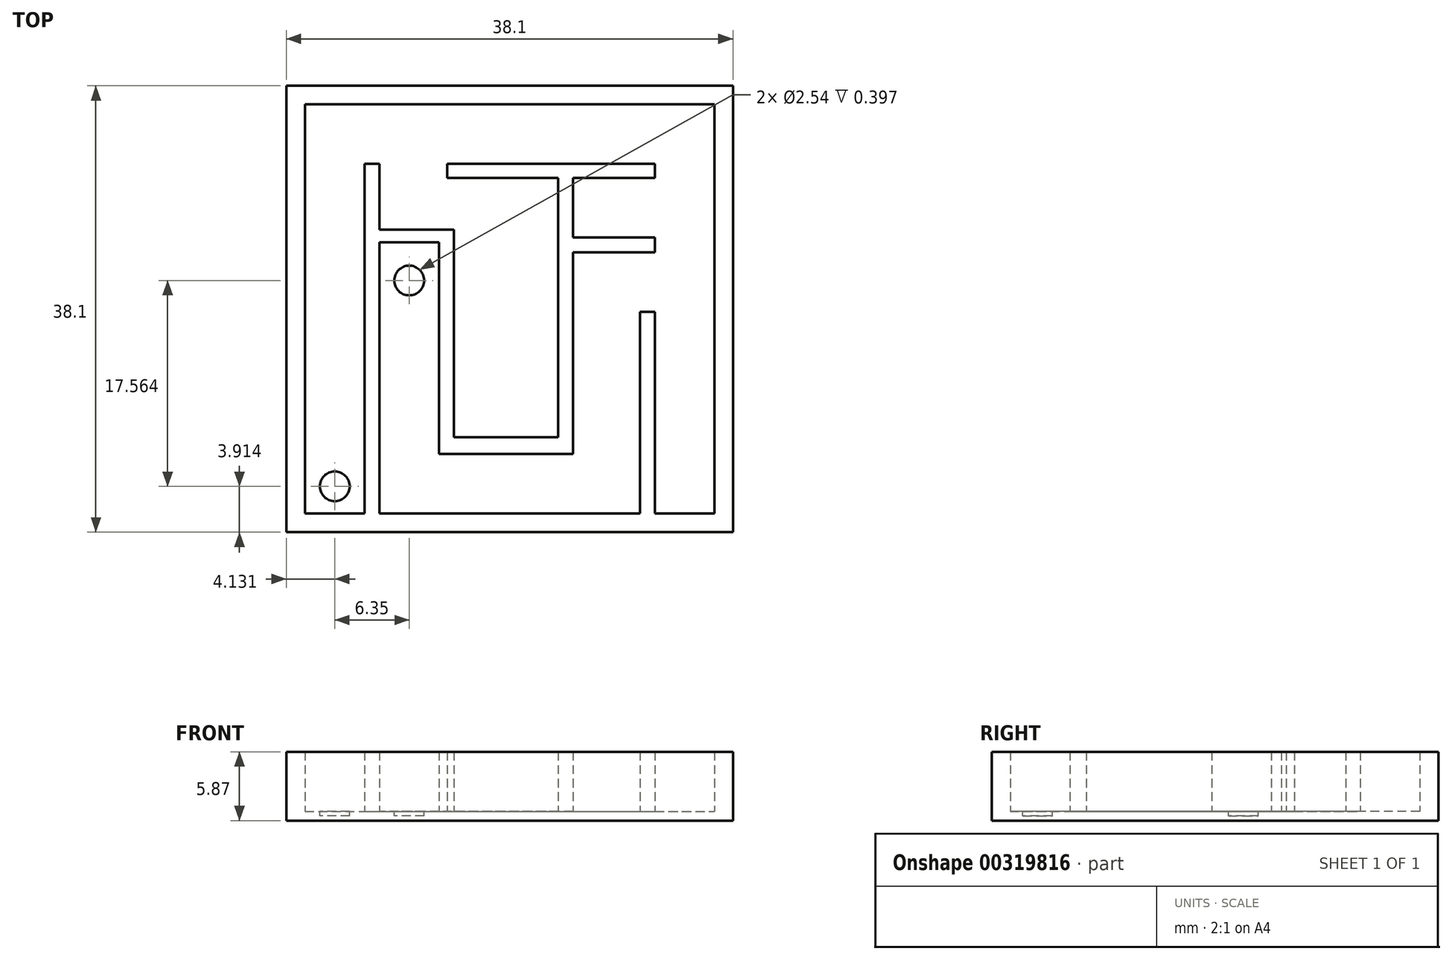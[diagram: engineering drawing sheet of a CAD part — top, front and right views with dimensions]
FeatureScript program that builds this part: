
annotation { "Feature Type Name" : "Feature", "Feature Type Description" : "" }
export const myFeature = defineFeature(function(context is Context, id is Id, definition is map)
    precondition{}
    {
        {
            var Q0;
            Q0=qCreatedBy(makeId("Top.planeOp"),FACE);
            var sketch = newSketch(context, id + "F0", { "sketchPlane" : qUnion([Q0])});
            skLineSegment(sketch, "E0.bottom", {"start": v(-35.55, 3.52) * mm, "end": v(2.55, 3.52) * mm});
            skLineSegment(sketch, "E0.top", {"start": v(-35.55, -34.58) * mm, "end": v(2.55, -34.58) * mm});
            skLineSegment(sketch, "E0.left", {"start": v(-35.55, 3.52) * mm, "end": v(-35.55, -34.58) * mm});
            skLineSegment(sketch, "E0.right", {"start": v(2.55, 3.52) * mm, "end": v(2.55, -34.58) * mm});
            skSolve(sketch);
        }
        {
            var Q0;
            Q0=makeQuery(id+"F0.imprint","IMPRINT",FACE,{"disambiguationData":[TD([[makeQuery(id+"F0.imprint","IMPRINT",EDGE,{"derivedFrom":sQuery(id+"F0.wireOp",EDGE,"E0.bottom")}),-1.0]])]});
            extrude(context, id + "F1", {"entities" : qUnion([Q0]), "depth" : 0.8 * mm});
        }
        {
            var Q0;
            Q0=makeQuery(id+"F1.opExtrude","CAP_FACE",FACE,{"disambiguationData":[OSD([sQuery(id+"F0.wireOp",EDGE,"E0.bottom"),sQuery(id+"F0.wireOp",EDGE,"E0.top"),sQuery(id+"F0.wireOp",EDGE,"E0.left"),sQuery(id+"F0.wireOp",EDGE,"E0.right")])],"isStart":false});
            var sketch = newSketch(context, id + "F2", { "sketchPlane" : qUnion([Q0])});
            skLineSegment(sketch, "E1.0", {"start": v(-33.96, 1.94) * mm, "end": v(0.97, 1.94) * mm});
            skLineSegment(sketch, "E1.1", {"start": v(-33.96, 1.94) * mm, "end": v(-33.96, -32.99) * mm});
            skLineSegment(sketch, "E1.2", {"start": v(-33.96, -32.99) * mm, "end": v(0.97, -32.99) * mm});
            skLineSegment(sketch, "E1.3", {"start": v(0.97, 1.94) * mm, "end": v(0.97, -32.99) * mm});
            skSolve(sketch);
        }
        {
            var Q0;
            Q0=makeQuery(id+"F2.imprint","IMPRINT",FACE,{"disambiguationData":[TD([[makeQuery(id+"F2.imprint","IMPRINT",EDGE,{"derivedFrom":sQuery(id+"F2.wireOp",EDGE,"E1.0")}),1.0]])]});
            extrude(context, id + "F3", {"entities" : qUnion([Q0]), "operationType" : NewBodyOperationType.ADD, "depth" : 5.08 * mm});
        }
        {
            var Q0;
            Q0=makeQuery(id+"F1.opExtrude","CAP_FACE",FACE,{"disambiguationData":[OSD([sQuery(id+"F0.wireOp",EDGE,"E0.bottom"),sQuery(id+"F0.wireOp",EDGE,"E0.top"),sQuery(id+"F0.wireOp",EDGE,"E0.left"),sQuery(id+"F0.wireOp",EDGE,"E0.right")])],"isStart":false});
            var sketch = newSketch(context, id + "F4", { "sketchPlane" : qUnion([Q0])});
            skLineSegment(sketch, "E2.bottom", {"start": v(-28.88, -32.99) * mm, "end": v(-27.6, -32.99) * mm});
            skLineSegment(sketch, "E2.top", {"start": v(-28.88, -3.14) * mm, "end": v(-27.6, -3.14) * mm});
            skLineSegment(sketch, "E2.left", {"start": v(-28.88, -32.99) * mm, "end": v(-28.88, -3.14) * mm});
            skLineSegment(sketch, "E2.right", {"start": v(-27.6, -32.99) * mm, "end": v(-27.6, -3.14) * mm});
            skSolve(sketch);
        }
        {
            var Q0;
            Q0=makeQuery(id+"F4.imprint","IMPRINT",FACE,{"disambiguationData":[TD([[makeQuery(id+"F4.imprint","IMPRINT",EDGE,{"derivedFrom":sQuery(id+"F4.wireOp",EDGE,"E2.bottom")}),1.0]])]});
            extrude(context, id + "F5", {"entities" : qUnion([Q0]), "operationType" : NewBodyOperationType.ADD, "depth" : 5.08 * mm});
        }
        {
            var Q0;
            Q0=makeQuery(id+"F1.opExtrude","CAP_FACE",FACE,{"disambiguationData":[OSD([sQuery(id+"F0.wireOp",EDGE,"E0.bottom"),sQuery(id+"F0.wireOp",EDGE,"E0.top"),sQuery(id+"F0.wireOp",EDGE,"E0.left"),sQuery(id+"F0.wireOp",EDGE,"E0.right")])],"isStart":false});
            var sketch = newSketch(context, id + "F6", { "sketchPlane" : qUnion([Q0])});
            skLineSegment(sketch, "E3", {"start": v(-33.96, -32.99) * mm, "end": v(-28.88, -32.99) * mm});
            skCircle(sketch, "E4", {"center": v(-31.42, -30.67) * mm, "radius": 1.27 * mm});
            skPoint(sketch, "E4.centerSnap0", {"position": v(-31.42, -32.99) * mm});
            skSolve(sketch);
        }
        {
            var Q0;
            Q0=makeQuery(id+"F6.imprint","IMPRINT",FACE,{"disambiguationData":[TD([[makeQuery(id+"F6.imprint","IMPRINT",EDGE,{"derivedFrom":sQuery(id+"F6.wireOp",EDGE,"E4")}),1.0]])]});
            extrude(context, id + "F7", {"entities" : qUnion([Q0]), "operationType" : NewBodyOperationType.REMOVE, "oppositeDirection" : true, "depth" : 0.4 * mm});
        }
        {
            var Q0;
            Q0=makeQuery(id+"F1.opExtrude","CAP_FACE",FACE,{"disambiguationData":[OSD([sQuery(id+"F0.wireOp",EDGE,"E0.bottom"),sQuery(id+"F0.wireOp",EDGE,"E0.top"),sQuery(id+"F0.wireOp",EDGE,"E0.left"),sQuery(id+"F0.wireOp",EDGE,"E0.right")])],"isStart":false});
            var sketch = newSketch(context, id + "F8", { "sketchPlane" : qUnion([Q0])});
            skLineSegment(sketch, "E5.bottom", {"start": v(-21.84, -3.14) * mm, "end": v(-4.11, -3.14) * mm});
            skLineSegment(sketch, "E5.top", {"start": v(-21.84, -4.36) * mm, "end": v(-12.37, -4.36) * mm});
            skLineSegment(sketch, "E5.left", {"start": v(-21.84, -3.14) * mm, "end": v(-21.84, -4.36) * mm});
            skLineSegment(sketch, "E5.right", {"start": v(-4.11, -3.14) * mm, "end": v(-4.11, -4.36) * mm});
            skLineSegment(sketch, "E6.trimOffspring", {"start": v(-11.1, -4.36) * mm, "end": v(-4.11, -4.36) * mm});
            skLineSegment(sketch, "E7.bottom", {"start": v(-5.38, -15.8) * mm, "end": v(-4.11, -15.8) * mm});
            skLineSegment(sketch, "E7.top", {"start": v(-5.38, -32.99) * mm, "end": v(-4.11, -32.99) * mm});
            skLineSegment(sketch, "E7.left", {"start": v(-5.38, -15.8) * mm, "end": v(-5.38, -32.99) * mm});
            skLineSegment(sketch, "E7.right", {"start": v(-4.11, -15.8) * mm, "end": v(-4.11, -32.99) * mm});
            skLineSegment(sketch, "E8", {"start": v(-12.37, -4.36) * mm, "end": v(-12.37, -26.5) * mm});
            skLineSegment(sketch, "E9.top", {"start": v(-12.37, -26.5) * mm, "end": v(-21.26, -26.5) * mm});
            skLineSegment(sketch, "E10.top", {"start": v(-22.53, -8.77) * mm, "end": v(-21.26, -8.77) * mm});
            skLineSegment(sketch, "E10.left", {"start": v(-22.53, -27.9) * mm, "end": v(-22.53, -9.85) * mm});
            skLineSegment(sketch, "E11.bottom", {"start": v(-21.26, -8.77) * mm, "end": v(-27.6, -8.77) * mm});
            skLineSegment(sketch, "E11.top", {"start": v(-22.53, -9.85) * mm, "end": v(-27.6, -9.85) * mm});
            skLineSegment(sketch, "E11.right", {"start": v(-27.6, -8.77) * mm, "end": v(-27.6, -9.85) * mm});
            skLineSegment(sketch, "E12", {"start": v(-21.26, -26.5) * mm, "end": v(-21.26, -8.77) * mm});
            skLineSegment(sketch, "E13", {"start": v(-11.1, -27.9) * mm, "end": v(-22.53, -27.9) * mm});
            skLineSegment(sketch, "E14", {"start": v(-11.1, -4.36) * mm, "end": v(-11.1, -27.9) * mm});
            skCircle(sketch, "E15", {"center": v(-25.07, -13.1) * mm, "radius": 1.27 * mm});
            skLineSegment(sketch, "E16.bottom", {"start": v(-11.1, -9.44) * mm, "end": v(-4.11, -9.44) * mm});
            skLineSegment(sketch, "E16.top", {"start": v(-11.1, -10.71) * mm, "end": v(-4.11, -10.71) * mm});
            skLineSegment(sketch, "E16.left", {"start": v(-11.1, -9.44) * mm, "end": v(-11.1, -10.71) * mm});
            skLineSegment(sketch, "E16.right", {"start": v(-4.11, -9.44) * mm, "end": v(-4.11, -10.71) * mm});
            skSolve(sketch);
        }
        {
            var Q0;
            Q0=makeQuery(id+"F8.imprint","IMPRINT",FACE,{"disambiguationData":[TD([[makeQuery(id+"F8.imprint","IMPRINT",EDGE,{"derivedFrom":sQuery(id+"F8.wireOp",EDGE,"E5.bottom")}),-1.0]])]});
            extrude(context, id + "F9", {"entities" : qUnion([Q0]), "operationType" : NewBodyOperationType.ADD, "depth" : 5.08 * mm});
        }
        {
            var Q0;
            Q0=makeQuery(id+"F8.imprint","IMPRINT",FACE,{"disambiguationData":[TD([[makeQuery(id+"F8.imprint","IMPRINT",EDGE,{"derivedFrom":sQuery(id+"F8.wireOp",EDGE,"E7.bottom")}),-1.0]])]});
            var Q1;
            Q1=makeQuery(id+"F8.imprint","IMPRINT",FACE,{"disambiguationData":[TD([[makeQuery(id+"F8.imprint","IMPRINT",EDGE,{"derivedFrom":sQuery(id+"F8.wireOp",EDGE,"Yuc0yRbK-59O8-SSbg-lOcn-BVCGj49pY7tD.bottom")}),1.0]])]});
            extrude(context, id + "F10", {"entities" : qUnion([Q0, Q1]), "operationType" : NewBodyOperationType.ADD, "depth" : 5.08 * mm});
        }
        {
            var Q0;
            Q0=makeQuery(id+"F8.imprint","IMPRINT",FACE,{"disambiguationData":[TD([[makeQuery(id+"F8.imprint","IMPRINT",EDGE,{"derivedFrom":sQuery(id+"F8.wireOp",EDGE,"E15")}),1.0]])]});
            extrude(context, id + "F11", {"entities" : qUnion([Q0]), "operationType" : NewBodyOperationType.REMOVE, "oppositeDirection" : true, "depth" : 0.4 * mm});
        }
        {
            var Q0;
            Q0=makeQuery(id+"F8.imprint","IMPRINT",FACE,{"disambiguationData":[TD([[makeQuery(id+"F8.imprint","IMPRINT",EDGE,{"derivedFrom":sQuery(id+"F8.wireOp",EDGE,"E16.bottom")}),-1.0]])]});
            extrude(context, id + "F12", {"entities" : qUnion([Q0]), "operationType" : NewBodyOperationType.ADD, "depth" : 5.08 * mm});
        }
    });
